# Revit family: ACCESS~1
name_source: partatom
category: Specialty Equipment
units: mm (PartAtom-declared; Revit-internal decimal feet)

## family parameters
Cut with Voids When Loaded = No
Host = Face
OmniClass Number = 23.31.25.00
Part Type = Normal
Room Calculation Point = No
Round Connector Dimension = Use Diameter
Shared = No

## types (4) — shared parameters
ADA Compliant = No
Assembly Code = C1030200
Date Modified = 08/17/2024
Default Elevation = 42"
Description = Handshower Bracket in Polished Chrome
Height = 2 1/8"
Length = 3 1/4"
Manufacturer = Kohler Co.
Master Format 2014 = 10 28 00
Master Format 2014 Name = Toilet, Bath, and Laundry Accessories
Material = Plastic
Product Documentation Link = http://resources.kohler.com
Product Name = Mastershower
URL = https://www.kohler.co.in
WaterSense Certified = No
Width = 3 1/8"

## per-type parameters (varying)
| type | Finish | Model | Product Page URL | Type |
| CP-Polished Chrome | Kohler-Plastic-CP-Polished_Chrome | K-9038IN-CP | https://www.kohler.co.in | 1 |
| BN-Vibrant Brushed Nickel | KOHLER-Plastic-BN-Vibrant_Brushed_Nickel | K-9038IN-BN | https://www.kohler.co.in | 2 |
| BV-Brushed Bronze | Kohler-Plastic-BV-Brushed_Bronze | K-9038IN-BV |  | 3 |
| BRD-Brushed Rose Gold | Kohler-Plastic-BRD-Brushed_Rose_Gold | K-9038IN-BRD |  | 4 |

## geometry (parser evidence)
native form markers: Sweep x6
no freeform markers — native parametric forms only
